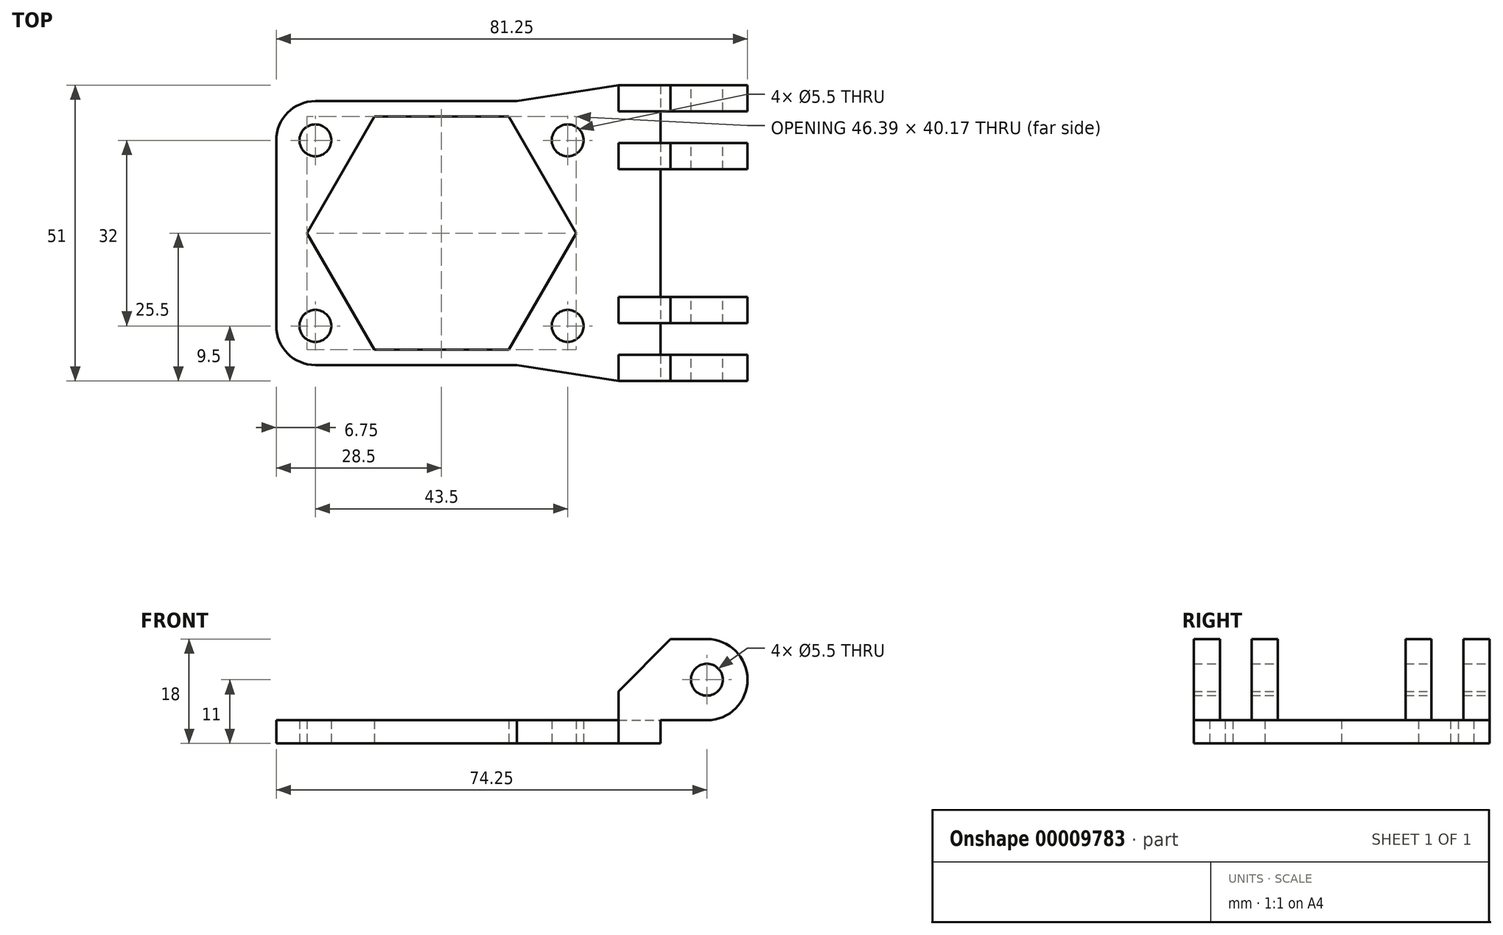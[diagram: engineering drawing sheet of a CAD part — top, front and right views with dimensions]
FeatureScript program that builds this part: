
annotation { "Feature Type Name" : "Feature", "Feature Type Description" : "" }
export const myFeature = defineFeature(function(context is Context, id is Id, definition is map)
    precondition{}
    {
        {
            var Q0;
            Q0=qCreatedBy(makeId("Top.planeOp"),FACE);
            var sketch = newSketch(context, id + "F0", { "sketchPlane" : qUnion([Q0])});
            skLineSegment(sketch, "E0.rect.bottom", {"start": v(37.75, -22.75) * mm, "end": v(-21.75, -22.75) * mm});
            skLineSegment(sketch, "E0.rect.top", {"start": v(37.75, 22.75) * mm, "end": v(-21.75, 22.75) * mm});
            skLineSegment(sketch, "E0.rect.right", {"start": v(-28.5, -16) * mm, "end": v(-28.5, 16) * mm});
            skPoint(sketch, "E0.rect.middle", {"position": v(0, 0) * mm});
            skCircle(sketch, "E1", {"center": v(-21.75, 16) * mm, "radius": 2.75 * mm});
            skCircle(sketch, "E2", {"center": v(21.75, 16) * mm, "radius": 2.75 * mm});
            skCircle(sketch, "E3", {"center": v(21.75, -16) * mm, "radius": 2.75 * mm});
            skCircle(sketch, "E4", {"center": v(-21.75, -16) * mm, "radius": 2.75 * mm});
            skCircle(sketch, "E5.cCircle", {"center": v(0, 0) * mm, "radius": 20.09 * mm, "construction": true});
            skLineSegment(sketch, "E5.0", {"start": v(23.2, 0) * mm, "end": v(11.6, -20.09) * mm});
            skLineSegment(sketch, "E5.1", {"start": v(11.6, -20.09) * mm, "end": v(-11.6, -20.09) * mm});
            skLineSegment(sketch, "E5.2", {"start": v(-11.6, -20.09) * mm, "end": v(-23.2, 0) * mm});
            skLineSegment(sketch, "E5.3", {"start": v(-23.2, 0) * mm, "end": v(-11.6, 20.09) * mm});
            skLineSegment(sketch, "E5.4", {"start": v(-11.6, 20.09) * mm, "end": v(11.6, 20.09) * mm});
            skLineSegment(sketch, "E5.5", {"start": v(11.6, 20.09) * mm, "end": v(23.2, 0) * mm});
            skPoint(sketch, "E5.0.midPoint", {"position": v(17.4, -10.04) * mm});
            skArc(sketch, "E6", {"start": v(-21.75, 22.75) * mm, "mid": v(-26.52, 20.77) * mm, "end": v(-28.5, 16) * mm});
            skArc(sketch, "E7", {"start": v(-28.5, -16) * mm, "mid": v(-26.52, -20.77) * mm, "end": v(-21.75, -22.75) * mm});
            skLineSegment(sketch, "E8", {"start": v(37.75, 22.75) * mm, "end": v(37.75, 0) * mm});
            skLineSegment(sketch, "E9", {"start": v(37.75, 0) * mm, "end": v(37.75, -22.75) * mm});
            skSolve(sketch);
        }
        {
            var Q0;
            Q0 = qSketchRegion(id + "F0", true);
            extrude(context, id + "F1", {"entities" : qUnion([Q0]), "depth" : 4 * mm});
        }
        {
            var Q0;
            Q0=makeQuery(id+"F1.opExtrude","CAP_FACE",FACE,{"disambiguationData":[OSD([sQuery(id+"F0.wireOp",EDGE,"E0.rect.bottom"),sQuery(id+"F0.wireOp",EDGE,"E0.rect.top"),sQuery(id+"F0.wireOp",EDGE,"E0.rect.right"),sQuery(id+"F0.wireOp",EDGE,"E1"),sQuery(id+"F0.wireOp",EDGE,"E2"),sQuery(id+"F0.wireOp",EDGE,"E3"),sQuery(id+"F0.wireOp",EDGE,"E4"),sQuery(id+"F0.wireOp",EDGE,"E5.0"),sQuery(id+"F0.wireOp",EDGE,"E5.1"),sQuery(id+"F0.wireOp",EDGE,"E5.2"),sQuery(id+"F0.wireOp",EDGE,"E5.3"),sQuery(id+"F0.wireOp",EDGE,"E5.4"),sQuery(id+"F0.wireOp",EDGE,"E5.5"),sQuery(id+"F0.wireOp",EDGE,"E6"),sQuery(id+"F0.wireOp",EDGE,"E7"),sQuery(id+"F0.wireOp",EDGE,"E8")])],"isStart":false});
            var sketch = newSketch(context, id + "F2", { "sketchPlane" : qUnion([Q0])});
            skLineSegment(sketch, "E10.bottom", {"start": v(30.5, 25.5) * mm, "end": v(52.75, 25.5) * mm});
            skLineSegment(sketch, "E10.top", {"start": v(30.5, 21) * mm, "end": v(52.75, 21) * mm});
            skLineSegment(sketch, "E10.left", {"start": v(30.5, 25.5) * mm, "end": v(30.5, 21) * mm});
            skLineSegment(sketch, "E10.right", {"start": v(52.75, 25.5) * mm, "end": v(52.75, 21) * mm});
            skLineSegment(sketch, "E11.left", {"start": v(30.5, 15.5) * mm, "end": v(30.5, 11) * mm});
            skLineSegment(sketch, "E11.top", {"start": v(30.5, 11) * mm, "end": v(52.75, 11) * mm});
            skLineSegment(sketch, "E11.bottom", {"start": v(30.5, 15.5) * mm, "end": v(52.75, 15.5) * mm});
            skLineSegment(sketch, "E11.right", {"start": v(52.75, 15.5) * mm, "end": v(52.75, 11) * mm});
            skLineSegment(sketch, "E12", {"start": v(52.75, 11) * mm, "end": v(52.75, 5.5) * mm, "construction": true});
            skLineSegment(sketch, "E13", {"start": v(52.75, 15.5) * mm, "end": v(52.75, 21) * mm, "construction": true});
            skLineSegment(sketch, "E14.0.MirrorCS", {"start": v(30.5, -25.5) * mm, "end": v(52.75, -25.5) * mm});
            skLineSegment(sketch, "E14.1.MirrorCS", {"start": v(30.5, -21) * mm, "end": v(52.75, -21) * mm});
            skLineSegment(sketch, "E14.2.MirrorCS", {"start": v(30.5, -25.5) * mm, "end": v(30.5, -21) * mm});
            skLineSegment(sketch, "E14.3.MirrorCS", {"start": v(52.75, -15.5) * mm, "end": v(52.75, -21) * mm, "construction": true});
            skLineSegment(sketch, "E14.4.MirrorCS", {"start": v(52.75, -11) * mm, "end": v(52.75, -5.5) * mm, "construction": true});
            skLineSegment(sketch, "E14.5.MirrorCS", {"start": v(30.5, -15.5) * mm, "end": v(30.5, -11) * mm});
            skLineSegment(sketch, "E14.6.MirrorCS", {"start": v(52.75, -25.5) * mm, "end": v(52.75, -21) * mm});
            skLineSegment(sketch, "E14.7.MirrorCS", {"start": v(52.75, -15.5) * mm, "end": v(52.75, -11) * mm});
            skLineSegment(sketch, "E14.8.MirrorCS", {"start": v(30.5, -11) * mm, "end": v(52.75, -11) * mm});
            skLineSegment(sketch, "E14.9.MirrorCS", {"start": v(30.5, -15.5) * mm, "end": v(52.75, -15.5) * mm});
            skSolve(sketch);
        }
        {
            var Q0;
            {var subQ3=sQuery(id+"F2.wireOp",EDGE,"22b14587-2863-4453-9190-b40f1af2baeb");Q0=makeQuery(id+"F2.imprint","IMPRINT",FACE,{"disambiguationData":[TD([[makeQuery(id+"F2.imprint","IMPRINT",EDGE,{"derivedFrom":subQ3}),1.0]])]});}
            var Q1;
            {var subQ8=sQuery(id+"F2.wireOp",EDGE,"E10.bottom");Q1=makeQuery(id+"F2.imprint","IMPRINT",FACE,{"disambiguationData":[TD([[makeQuery(id+"F2.imprint","IMPRINT",EDGE,{"derivedFrom":subQ8}),-1.0]])]});}
            var Q2;
            {var subQ5=sQuery(id+"F2.wireOp",EDGE,"E11.right");Q2=makeQuery(id+"F2.imprint","IMPRINT",FACE,{"disambiguationData":[TD([[makeQuery(id+"F2.imprint","IMPRINT",EDGE,{"derivedFrom":subQ5}),-1.0]])]});}
            var Q3;
            {var subQ5=sQuery(id+"F2.wireOp",EDGE,"E14.7.MirrorCS");Q3=makeQuery(id+"F2.imprint","IMPRINT",FACE,{"disambiguationData":[TD([[makeQuery(id+"F2.imprint","IMPRINT",EDGE,{"derivedFrom":subQ5}),1.0]])]});}
            var Q4;
            {var subQ8=sQuery(id+"F2.wireOp",EDGE,"E14.0.MirrorCS");Q4=makeQuery(id+"F2.imprint","IMPRINT",FACE,{"disambiguationData":[TD([[makeQuery(id+"F2.imprint","IMPRINT",EDGE,{"derivedFrom":subQ8}),1.0]])]});}
            var Q5;
            {var subQ3=sQuery(id+"F2.wireOp",EDGE,"d45da9b8-bd1a-45a6-b1ff-c2ce73eec5f1");Q5=makeQuery(id+"F2.imprint","IMPRINT",FACE,{"disambiguationData":[TD([[makeQuery(id+"F2.imprint","IMPRINT",EDGE,{"derivedFrom":subQ3}),-1.0]])]});}
            var Q6;
            {var subQ5=sQuery(id+"F2.wireOp",EDGE,"E14.5.MirrorCS");Q6=makeQuery(id+"F2.imprint","IMPRINT",FACE,{"disambiguationData":[TD([[makeQuery(id+"F2.imprint","IMPRINT",EDGE,{"derivedFrom":subQ5}),-1.0]])]});}
            var Q7;
            {var subQ1=sQuery(id+"F2.wireOp",EDGE,"E14.1.MirrorCS");var subQ5=sQuery(id+"F2.wireOp",EDGE,"E14.2.MirrorCS");var subQ7=makeQuery(id+"F2.imprint","INTERSECT",VERTEX,{"derivedFrom":[subQ1,subQ5]});Q7=makeQuery(id+"F2.imprint","IMPRINT",FACE,{"disambiguationData":[TD([[makeQuery(id+"F2.imprint","IMPRINT",EDGE,{"disambiguationData":[TD([[subQ7,1.0]])],"derivedFrom":subQ5}),-1.0]])]});}
            var Q8;
            {var subQ5=sQuery(id+"F2.wireOp",EDGE,"E11.left");Q8=makeQuery(id+"F2.imprint","IMPRINT",FACE,{"disambiguationData":[TD([[makeQuery(id+"F2.imprint","IMPRINT",EDGE,{"derivedFrom":subQ5}),1.0]])]});}
            var Q9;
            {var subQ1=sQuery(id+"F2.wireOp",EDGE,"E10.top");var subQ5=sQuery(id+"F2.wireOp",EDGE,"E10.left");var subQ7=makeQuery(id+"F2.imprint","INTERSECT",VERTEX,{"derivedFrom":[subQ1,subQ5]});Q9=makeQuery(id+"F2.imprint","IMPRINT",FACE,{"disambiguationData":[TD([[makeQuery(id+"F2.imprint","IMPRINT",EDGE,{"disambiguationData":[TD([[subQ7,1.0]])],"derivedFrom":subQ5}),1.0]])]});}
            extrude(context, id + "F3", {"entities" : qUnion([Q0, Q1, Q2, Q3, Q4, Q5, Q6, Q7, Q8, Q9]), "operationType" : NewBodyOperationType.ADD, "depth" : (6 + 4 * 2) * mm});
        }
        {
            var Q0;
            Q0=makeQuery(id+"F3.opExtrude","CAP_EDGE",EDGE,{"disambiguationData":[OSD([sQuery(id+"F2.wireOp",EDGE,"E10.right")])],"isStart":false});
            var Q1;
            Q1=makeQuery(id+"F3.opExtrude","CAP_EDGE",EDGE,{"disambiguationData":[OSD([sQuery(id+"F2.wireOp",EDGE,"E11.right")])],"isStart":false});
            var Q2;
            Q2=makeQuery(id+"F3.opExtrude","CAP_EDGE",EDGE,{"disambiguationData":[OSD([sQuery(id+"F2.wireOp",EDGE,"E11.right")])],"isStart":true});
            var Q3;
            Q3=makeQuery(id+"F3.opExtrude","CAP_EDGE",EDGE,{"disambiguationData":[OSD([sQuery(id+"F2.wireOp",EDGE,"E10.right")])],"isStart":true});
            var Q4;
            Q4=makeQuery(id+"F3.opExtrude","CAP_EDGE",EDGE,{"disambiguationData":[OSD([sQuery(id+"F2.wireOp",EDGE,"E14.7.MirrorCS")])],"isStart":true});
            var Q5;
            Q5=makeQuery(id+"F3.opExtrude","CAP_EDGE",EDGE,{"disambiguationData":[OSD([sQuery(id+"F2.wireOp",EDGE,"E14.7.MirrorCS")])],"isStart":false});
            var Q6;
            Q6=makeQuery(id+"F3.opExtrude","CAP_EDGE",EDGE,{"disambiguationData":[OSD([sQuery(id+"F2.wireOp",EDGE,"E14.6.MirrorCS")])],"isStart":false});
            var Q7;
            Q7=makeQuery(id+"F3.opExtrude","CAP_EDGE",EDGE,{"disambiguationData":[OSD([sQuery(id+"F2.wireOp",EDGE,"E14.6.MirrorCS")])],"isStart":true});
            fillet(context, id + "F4", {"entities" : qUnion([Q0, Q1, Q2, Q3, Q4, Q5, Q6, Q7]), "radius" : 7 * mm, "tangentPropagation" : true, "allowEdgeOverflow" : false});
        }
        {
            var Q0;
            Q0=qCreatedBy(makeId("Front.planeOp"),FACE);
            var sketch = newSketch(context, id + "F5", { "sketchPlane" : qUnion([Q0])});
            skCircle(sketch, "E15", {"center": v(45.75, 11) * mm, "radius": 2.75 * mm});
            skLineSegment(sketch, "E16", {"start": v(45.75, 11) * mm, "end": v(45.75, 18) * mm});
            skLineSegment(sketch, "E17", {"start": v(45.75, 11) * mm, "end": v(52.75, 11) * mm});
            skLineSegment(sketch, "E18", {"start": v(45.75, 11) * mm, "end": v(45.75, 4) * mm});
            skSolve(sketch);
        }
        {
            var Q0;
            Q0=makeQuery(id+"F5.imprint","IMPRINT",FACE,{"disambiguationData":[TD([[makeQuery(id+"F5.imprint","IMPRINT",EDGE,{"derivedFrom":sQuery(id+"F5.wireOp",EDGE,"E15")}),1.0]])]});
            var Q1;
            Q1=sQuery(id+"F5.wireOp",EDGE,"E15");
            extrude(context, id + "F6", {"entities" : qUnion([Q0]), "operationType" : NewBodyOperationType.REMOVE, "surfaceEntities" : qUnion([Q1]), "endBound" : BoundingType.THROUGH_ALL, "depth" : 25 * mm, "hasSecondDirection" : true, "secondDirectionBound" : SecondDirectionBoundingType.THROUGH_ALL, "secondDirectionOppositeDirection" : true, "secondDirectionDepth" : 25 * mm});
        }
        {
            var Q0;
            Q0=qCreatedBy(makeId("Top.planeOp"),FACE);
            var sketch = newSketch(context, id + "F7", { "sketchPlane" : qUnion([Q0])});
            skLineSegment(sketch, "E19", {"start": v(12.97, 22.75) * mm, "end": v(30.5, 25.5) * mm});
            skLineSegment(sketch, "E20", {"start": v(30.5, 25.5) * mm, "end": v(37.75, 25.5) * mm});
            skLineSegment(sketch, "E21", {"start": v(30.5, -25.5) * mm, "end": v(12.97, -22.75) * mm});
            skLineSegment(sketch, "E22", {"start": v(12.97, -22.75) * mm, "end": v(29.64, -20.6) * mm});
            skLineSegment(sketch, "E23", {"start": v(37.75, -25.5) * mm, "end": v(30.5, -25.5) * mm});
            skPoint(sketch, "E24.visualSharp", {"position": v(37.75, 15.63) * mm});
            skLineSegment(sketch, "E25", {"start": v(29.64, 20.6) * mm, "end": v(12.97, 22.75) * mm});
            skLineSegment(sketch, "E26", {"start": v(29.64, -20.6) * mm, "end": v(29.64, 20.6) * mm});
            skLineSegment(sketch, "E27", {"start": v(37.75, 25.5) * mm, "end": v(37.75, -25.5) * mm});
            skSolve(sketch);
        }
        {
            var Q0;
            Q0=makeQuery(id+"F7.imprint","IMPRINT",FACE,{"disambiguationData":[TD([[makeQuery(id+"F7.imprint","IMPRINT",EDGE,{"derivedFrom":sQuery(id+"F7.wireOp",EDGE,"E19")}),-1.0]])]});
            extrude(context, id + "F8", {"entities" : qUnion([Q0]), "operationType" : NewBodyOperationType.ADD, "depth" : 4 * mm});
        }
        {
            var Q0;
            Q0=makeQuery(id+"F3.opExtrude","CAP_EDGE",EDGE,{"disambiguationData":[OSD([sQuery(id+"F2.wireOp",EDGE,"E10.left")])],"isStart":false});
            var Q1;
            Q1=makeQuery(id+"F3.opExtrude","CAP_EDGE",EDGE,{"disambiguationData":[OSD([sQuery(id+"F2.wireOp",EDGE,"E11.left")])],"isStart":false});
            var Q2;
            Q2=makeQuery(id+"F3.opExtrude","CAP_EDGE",EDGE,{"disambiguationData":[OSD([sQuery(id+"F2.wireOp",EDGE,"E14.5.MirrorCS")])],"isStart":false});
            var Q3;
            Q3=makeQuery(id+"F3.opExtrude","CAP_EDGE",EDGE,{"disambiguationData":[OSD([sQuery(id+"F2.wireOp",EDGE,"E14.2.MirrorCS")])],"isStart":false});
            chamfer(context, id + "F9", {"entities" : qUnion([Q0, Q1, Q2, Q3]), "width" : 9 * mm, "tangentPropagation" : true});
        }
    });
